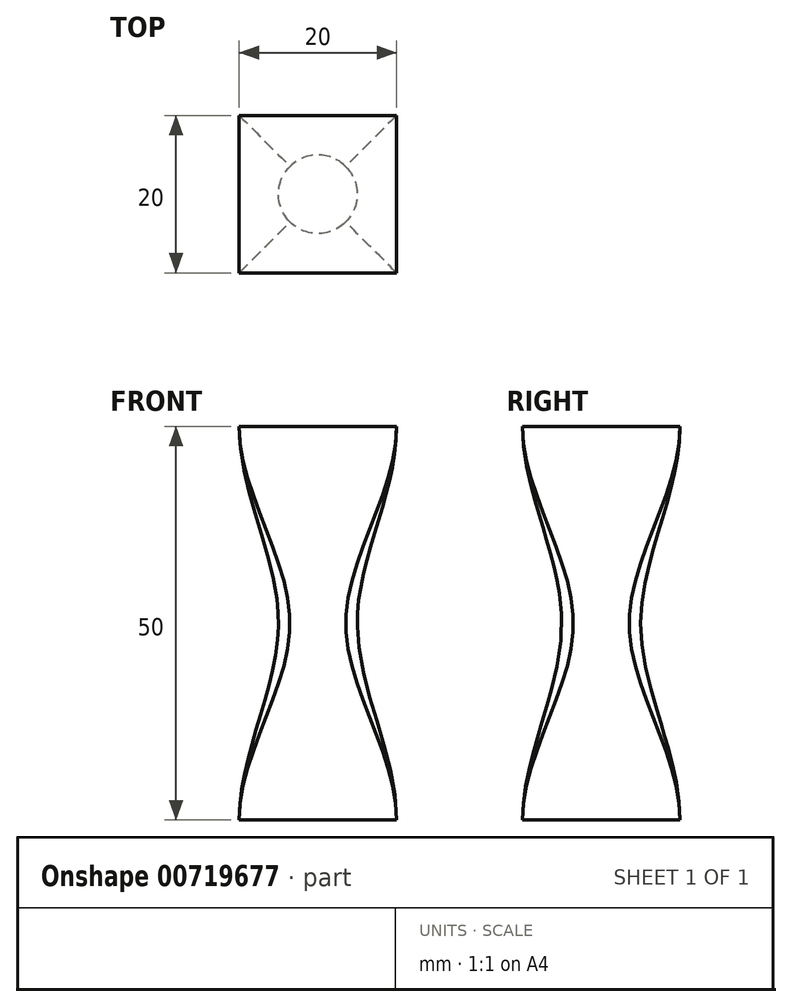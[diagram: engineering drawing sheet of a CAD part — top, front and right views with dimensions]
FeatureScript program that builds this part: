
annotation { "Feature Type Name" : "Feature", "Feature Type Description" : "" }
export const myFeature = defineFeature(function(context is Context, id is Id, definition is map)
    precondition{}
    {
        {
            var Q0;
            Q0=qCreatedBy(makeId("Top.planeOp"),FACE);
            var sketch = newSketch(context, id + "F0", { "sketchPlane" : qUnion([Q0])});
            skLineSegment(sketch, "E0.bottom", {"start": v(-10, 10) * mm, "end": v(10, 10) * mm});
            skLineSegment(sketch, "E0.top", {"start": v(-10, -10) * mm, "end": v(10, -10) * mm});
            skLineSegment(sketch, "E0.left", {"start": v(-10, 10) * mm, "end": v(-10, -10) * mm});
            skLineSegment(sketch, "E0.right", {"start": v(10, 10) * mm, "end": v(10, -10) * mm});
            skPoint(sketch, "E0.middle", {"position": v(0, 0) * mm});
            skSolve(sketch);
        }
        {
            var Q0;
            Q0=qCreatedBy(makeId("Top.planeOp"),FACE);
            cPlane(context, id + "F1", {"entities" : qUnion([Q0]), "cplaneType" : CPlaneType.OFFSET, "offset" : 25 * mm, "oppositeDirection" : true, "width" : 150 * mm, "height" : 150 * mm});
        }
        {
            var Q0;
            Q0=qCreatedBy(id+"F1.planeOp",FACE);
            var sketch = newSketch(context, id + "F2", { "sketchPlane" : qUnion([Q0])});
            skCircle(sketch, "E1", {"center": v(0, 0) * mm, "radius": 5 * mm});
            skSolve(sketch);
        }
        {
            var Q0;
            Q0=qCreatedBy(makeId("Top.planeOp"),FACE);
            cPlane(context, id + "F3", {"entities" : qUnion([Q0]), "cplaneType" : CPlaneType.OFFSET, "offset" : 50 * mm, "oppositeDirection" : true, "width" : 150 * mm, "height" : 150 * mm});
        }
        {
            var Q0;
            Q0=qCreatedBy(id+"F3.planeOp",FACE);
            var sketch = newSketch(context, id + "F4", { "sketchPlane" : qUnion([Q0])});
            skLineSegment(sketch, "E2.0.0", {"start": v(-10, 10) * mm, "end": v(-10, -10) * mm});
            skLineSegment(sketch, "E2.0.1", {"start": v(-10, -10) * mm, "end": v(10, -10) * mm});
            skLineSegment(sketch, "E2.0.2", {"start": v(10, -10) * mm, "end": v(10, 10) * mm});
            skLineSegment(sketch, "E2.0.3", {"start": v(10, 10) * mm, "end": v(-10, 10) * mm});
            skSolve(sketch);
        }
        {
            var Q0;
            Q0=makeQuery(id+"F4.imprint","IMPRINT",FACE,{"disambiguationData":[TD([[makeQuery(id+"F4.imprint","IMPRINT",EDGE,{"derivedFrom":sQuery(id+"F4.wireOp",EDGE,"E2.0.0")}),1.0]])]});
            var Q1;
            Q1=makeQuery(id+"F2.imprint","IMPRINT",FACE,{"disambiguationData":[TD([[makeQuery(id+"F2.imprint","IMPRINT",EDGE,{"derivedFrom":sQuery(id+"F2.wireOp",EDGE,"E1")}),1.0]])]});
            var Q2;
            Q2=makeQuery(id+"F0.imprint","IMPRINT",FACE,{"disambiguationData":[TD([[makeQuery(id+"F0.imprint","IMPRINT",EDGE,{"derivedFrom":sQuery(id+"F0.wireOp",EDGE,"E0.bottom")}),-1.0]])]});
            loft(context, id + "F5", {"startCondition" : LoftEndDerivativeType.NORMAL_TO_PROFILE, "startMagnitude" : 1, "endCondition" : LoftEndDerivativeType.NORMAL_TO_PROFILE, "endMagnitude" : 1, "sheetProfilesArray" : [{ "sheetProfileEntities" : qUnion([Q0]) }, { "sheetProfileEntities" : qUnion([Q1]) }, { "sheetProfileEntities" : qUnion([Q2]) }]});
        }
    });
